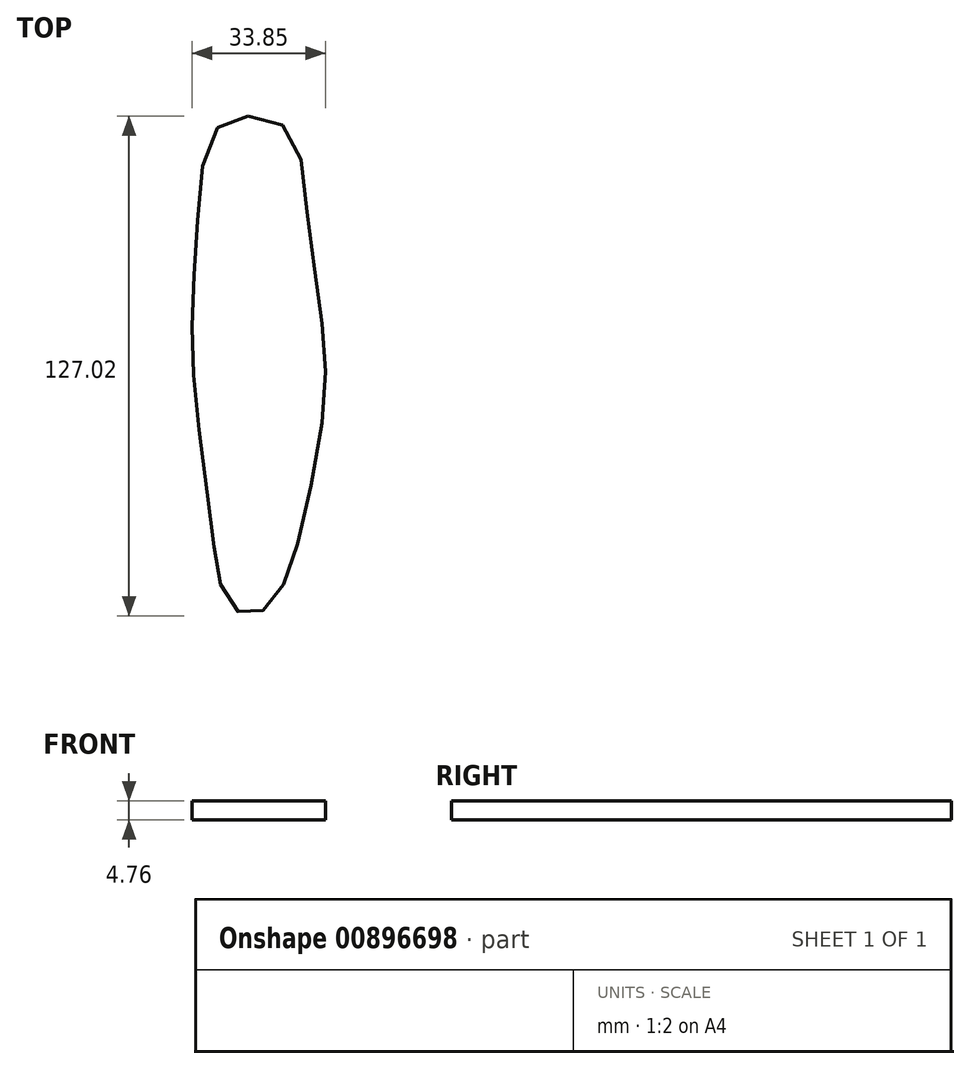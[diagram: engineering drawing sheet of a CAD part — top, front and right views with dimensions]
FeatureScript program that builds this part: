
annotation { "Feature Type Name" : "Feature", "Feature Type Description" : "" }
export const myFeature = defineFeature(function(context is Context, id is Id, definition is map)
    precondition{}
    {
        {
            var Q0;
            Q0=qCreatedBy(makeId("Top.planeOp"),FACE);
            var sketch = newSketch(context, id + "F0", { "sketchPlane" : qUnion([Q0])});
            skFitSpline(sketch, "E0", {"points": [v(0, 76.61) * mm, v(-8.63, 72.47) * mm, v(-12.77, 50.39) * mm, v(-14.15, 24.16) * mm, v(-12.77, 0) * mm, v(-8.63, -32.44) * mm, v(-5.87, -44.86) * mm, v(0, -50.39) * mm, v(6.56, -46.24) * mm, v(12.08, -33.82) * mm, v(18.98, 0) * mm, v(18.98, 22.78) * mm, v(15.14, 51.78) * mm, v(10.7, 72.47) * mm, v(0, 76.61) * mm]});
            skSolve(sketch);
        }
        {
            var Q0;
            Q0=sQuery(id+"F0.wireOp",EDGE,"E0");
            extrude(context, id + "F1", {"bodyType" : ToolBodyType.SURFACE, "surfaceEntities" : qUnion([Q0]), "depth" : 4.76 * mm, "offsetDistance" : 25.4 * mm});
        }
    });
